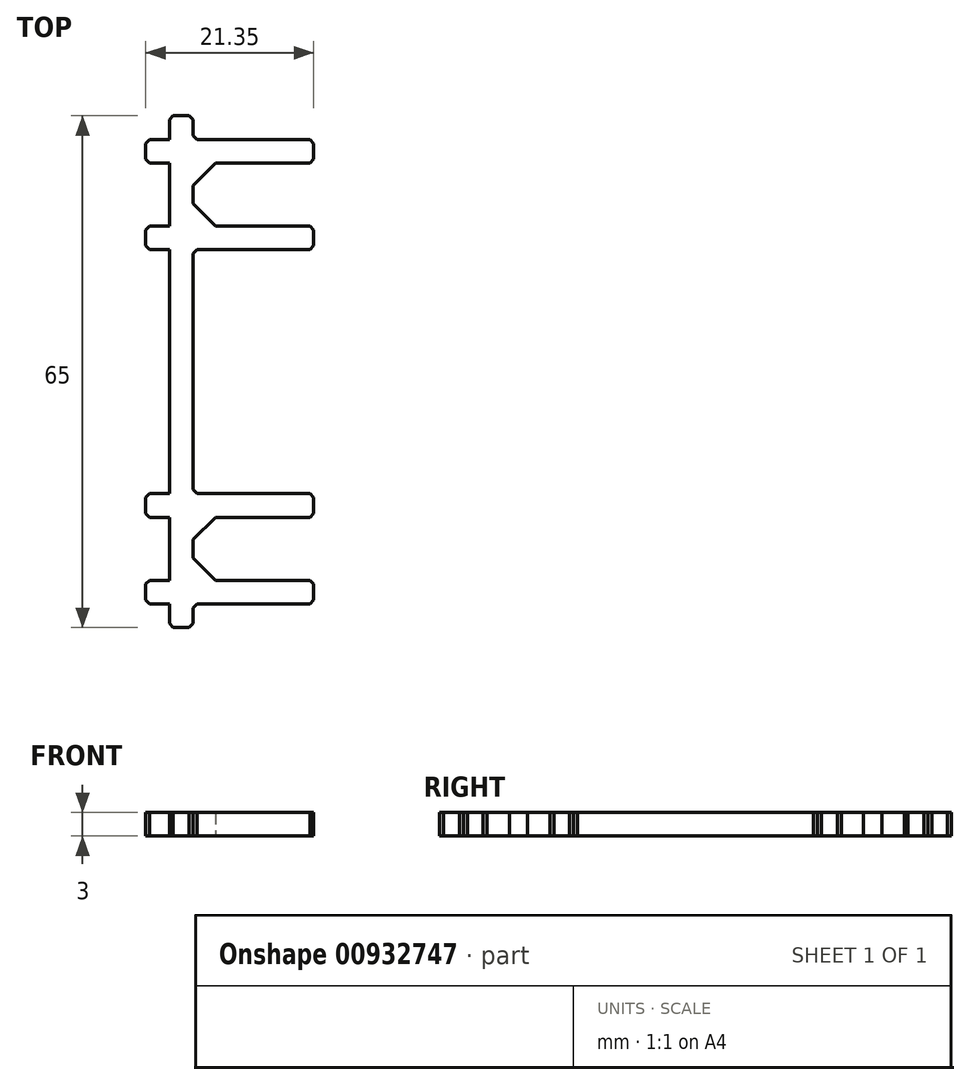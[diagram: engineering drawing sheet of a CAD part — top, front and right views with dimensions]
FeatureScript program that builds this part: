
annotation { "Feature Type Name" : "Feature", "Feature Type Description" : "" }
export const myFeature = defineFeature(function(context is Context, id is Id, definition is map)
    precondition{}
    {
        {
            var Q0;
            Q0=qCreatedBy(makeId("Top.planeOp"),FACE);
            var sketch = newSketch(context, id + "F0", { "sketchPlane" : qUnion([Q0])});
            skLineSegment(sketch, "E0", {"start": v(8.84, 26.5) * mm, "end": v(6, 23.66) * mm});
            skLineSegment(sketch, "E1", {"start": v(6, 21.34) * mm, "end": v(8.84, 18.5) * mm});
            skLineSegment(sketch, "E2", {"start": v(6, 23.66) * mm, "end": v(6, 21.34) * mm});
            skLineSegment(sketch, "E3", {"start": v(3, 26.5) * mm, "end": v(3, 18.5) * mm});
            skLineSegment(sketch, "E4", {"start": v(3, 15.5) * mm, "end": v(3, 0) * mm});
            skLineSegment(sketch, "E5", {"start": v(3, 29.5) * mm, "end": v(3, 32.5) * mm});
            skLineSegment(sketch, "E6", {"start": v(6, 15.5) * mm, "end": v(6, 0) * mm});
            skLineSegment(sketch, "E7", {"start": v(3, 18.5) * mm, "end": v(0, 18.5) * mm});
            skLineSegment(sketch, "E8", {"start": v(3, 15.5) * mm, "end": v(0, 15.5) * mm});
            skLineSegment(sketch, "E9", {"start": v(0, 15.5) * mm, "end": v(0, 18.5) * mm});
            skLineSegment(sketch, "E10", {"start": v(6, 15.5) * mm, "end": v(21.35, 15.5) * mm});
            skLineSegment(sketch, "E11", {"start": v(21.35, 15.5) * mm, "end": v(21.35, 18.5) * mm});
            skLineSegment(sketch, "E12", {"start": v(21.35, 18.5) * mm, "end": v(8.84, 18.5) * mm});
            skLineSegment(sketch, "E13", {"start": v(6, 29.5) * mm, "end": v(21.35, 29.5) * mm});
            skLineSegment(sketch, "E14", {"start": v(21.35, 29.5) * mm, "end": v(21.35, 26.5) * mm});
            skLineSegment(sketch, "E15", {"start": v(21.35, 26.5) * mm, "end": v(8.84, 26.5) * mm});
            skLineSegment(sketch, "E16", {"start": v(6, 32.5) * mm, "end": v(6, 29.5) * mm});
            skLineSegment(sketch, "E17", {"start": v(3, 32.5) * mm, "end": v(6, 32.5) * mm});
            skLineSegment(sketch, "E18", {"start": v(3, 29.5) * mm, "end": v(0, 29.5) * mm});
            skLineSegment(sketch, "E19", {"start": v(0, 29.5) * mm, "end": v(0, 26.5) * mm});
            skLineSegment(sketch, "E20", {"start": v(0, 26.5) * mm, "end": v(3, 26.5) * mm});
            skLineSegment(sketch, "E21", {"start": v(3, 0) * mm, "end": v(6, 0) * mm});
            skCircle(sketch, "E22", {"center": v(10.5, 22.5) * mm, "radius": 4 * mm, "construction": true});
            skLineSegment(sketch, "E23", {"start": v(6, 22.5) * mm, "end": v(10.5, 22.5) * mm, "construction": true});
            skSolve(sketch);
        }
        {
            var Q0;
            Q0=qSketchRegion(id+"F0",true);
            extrude(context, id + "F1", {"entities" : qUnion([Q0]), "depth" : 3 * mm, "offsetDistance" : 25 * mm});
        }
        {
            var Q0;
            Q0=makeQuery(id+"F1.opExtrude","SWEPT_EDGE",EDGE,{"disambiguationData":[OSD([sQuery(id+"F0.wireOp",EDGE,"E18"),sQuery(id+"F0.wireOp",EDGE,"E19")])]});
            var Q1;
            Q1=makeQuery(id+"F1.opExtrude","SWEPT_EDGE",EDGE,{"disambiguationData":[OSD([sQuery(id+"F0.wireOp",EDGE,"E19"),sQuery(id+"F0.wireOp",EDGE,"E20")])]});
            var Q2;
            Q2=makeQuery(id+"F1.opExtrude","SWEPT_EDGE",EDGE,{"disambiguationData":[OSD([sQuery(id+"F0.wireOp",EDGE,"E7"),sQuery(id+"F0.wireOp",EDGE,"E9")])]});
            var Q3;
            Q3=makeQuery(id+"F1.opExtrude","SWEPT_EDGE",EDGE,{"disambiguationData":[OSD([sQuery(id+"F0.wireOp",EDGE,"E8"),sQuery(id+"F0.wireOp",EDGE,"E9")])]});
            var Q4;
            Q4=makeQuery(id+"F1.opExtrude","SWEPT_EDGE",EDGE,{"disambiguationData":[OSD([sQuery(id+"F0.wireOp",EDGE,"E10"),sQuery(id+"F0.wireOp",EDGE,"E11")])]});
            var Q5;
            Q5=makeQuery(id+"F1.opExtrude","SWEPT_EDGE",EDGE,{"disambiguationData":[OSD([sQuery(id+"F0.wireOp",EDGE,"E14"),sQuery(id+"F0.wireOp",EDGE,"E15")])]});
            var Q6;
            Q6=makeQuery(id+"F1.opExtrude","SWEPT_EDGE",EDGE,{"disambiguationData":[OSD([sQuery(id+"F0.wireOp",EDGE,"E5"),sQuery(id+"F0.wireOp",EDGE,"E17")])]});
            var Q7;
            Q7=makeQuery(id+"F1.opExtrude","SWEPT_EDGE",EDGE,{"disambiguationData":[OSD([sQuery(id+"F0.wireOp",EDGE,"E16"),sQuery(id+"F0.wireOp",EDGE,"E17")])]});
            var Q8;
            Q8=makeQuery(id+"F1.opExtrude","SWEPT_EDGE",EDGE,{"disambiguationData":[OSD([sQuery(id+"F0.wireOp",EDGE,"E13"),sQuery(id+"F0.wireOp",EDGE,"E14")])]});
            var Q9;
            Q9=makeQuery(id+"F1.opExtrude","SWEPT_EDGE",EDGE,{"disambiguationData":[OSD([sQuery(id+"F0.wireOp",EDGE,"E11"),sQuery(id+"F0.wireOp",EDGE,"E12")])]});
            var Q10;
            Q10=makeQuery(id+"F1.opExtrude","SWEPT_EDGE",EDGE,{"disambiguationData":[OSD([sQuery(id+"F0.wireOp",EDGE,"E6"),sQuery(id+"F0.wireOp",EDGE,"E10")])]});
            var Q11;
            Q11=makeQuery(id+"F1.opExtrude","SWEPT_EDGE",EDGE,{"disambiguationData":[OSD([sQuery(id+"F0.wireOp",EDGE,"E13"),sQuery(id+"F0.wireOp",EDGE,"E16")])]});
            chamfer(context, id + "F2", {"entities" : qUnion([Q0, Q1, Q2, Q3, Q4, Q5, Q6, Q7, Q8, Q9, Q10, Q11]), "width" : 0.5 * mm, "tangentPropagation" : true});
        }
        {
            var Q0;
            Q0=makeQuery(id+"F1.opExtrude","SWEPT_BODY",BODY,{"disambiguationData":[OSD([sQuery(id+"F0.wireOp",EDGE,"E0"),sQuery(id+"F0.wireOp",EDGE,"E1"),sQuery(id+"F0.wireOp",EDGE,"E2"),sQuery(id+"F0.wireOp",EDGE,"E3"),sQuery(id+"F0.wireOp",EDGE,"E4"),sQuery(id+"F0.wireOp",EDGE,"E5"),sQuery(id+"F0.wireOp",EDGE,"E6"),sQuery(id+"F0.wireOp",EDGE,"E7"),sQuery(id+"F0.wireOp",EDGE,"E8"),sQuery(id+"F0.wireOp",EDGE,"E9"),sQuery(id+"F0.wireOp",EDGE,"E10"),sQuery(id+"F0.wireOp",EDGE,"E11"),sQuery(id+"F0.wireOp",EDGE,"E12"),sQuery(id+"F0.wireOp",EDGE,"E13"),sQuery(id+"F0.wireOp",EDGE,"E14"),sQuery(id+"F0.wireOp",EDGE,"E15"),sQuery(id+"F0.wireOp",EDGE,"E16"),sQuery(id+"F0.wireOp",EDGE,"E17"),sQuery(id+"F0.wireOp",EDGE,"E18"),sQuery(id+"F0.wireOp",EDGE,"E19"),sQuery(id+"F0.wireOp",EDGE,"E20"),sQuery(id+"F0.wireOp",EDGE,"E21")])]});
            var Q1;
            Q1=makeQuery(id+"F1.opExtrude","SWEPT_FACE",FACE,{"disambiguationData":[OSD([sQuery(id+"F0.wireOp",EDGE,"E21")])]});
            mirror(context, id + "F3", {"operationType" : NewBodyOperationType.ADD, "entities" : qUnion([Q0]), "mirrorPlane" : qUnion([Q1])});
        }
        {
            var Q0;
            {var subQ0=makeQuery(id+"F1.opExtrude","CAP_FACE",FACE,{"disambiguationData":[OSD([sQuery(id+"F0.wireOp",EDGE,"E0"),sQuery(id+"F0.wireOp",EDGE,"E1"),sQuery(id+"F0.wireOp",EDGE,"E2"),sQuery(id+"F0.wireOp",EDGE,"E3"),sQuery(id+"F0.wireOp",EDGE,"E4"),sQuery(id+"F0.wireOp",EDGE,"E5"),sQuery(id+"F0.wireOp",EDGE,"E6"),sQuery(id+"F0.wireOp",EDGE,"E7"),sQuery(id+"F0.wireOp",EDGE,"E8"),sQuery(id+"F0.wireOp",EDGE,"E9"),sQuery(id+"F0.wireOp",EDGE,"E10"),sQuery(id+"F0.wireOp",EDGE,"E11"),sQuery(id+"F0.wireOp",EDGE,"E12"),sQuery(id+"F0.wireOp",EDGE,"E13"),sQuery(id+"F0.wireOp",EDGE,"E14"),sQuery(id+"F0.wireOp",EDGE,"E15"),sQuery(id+"F0.wireOp",EDGE,"E16"),sQuery(id+"F0.wireOp",EDGE,"E17"),sQuery(id+"F0.wireOp",EDGE,"E18"),sQuery(id+"F0.wireOp",EDGE,"E19"),sQuery(id+"F0.wireOp",EDGE,"E20"),sQuery(id+"F0.wireOp",EDGE,"E21")])],"isStart":false});Q0=makeQuery(id+"F3.boolean.opBoolean","MERGE",FACE,{"derivedFrom":[subQ0,makeQuery(id+"F3.opPattern","COPY",FACE,{"derivedFrom":subQ0,"instanceName":"1"})]});}
            var sketch = newSketch(context, id + "F4", { "sketchPlane" : qUnion([Q0])});
            skCircle(sketch, "E24", {"center": v(10.5, 22.5) * mm, "radius": 4 * mm, "construction": true});
            skSolve(sketch);
        }
    });
